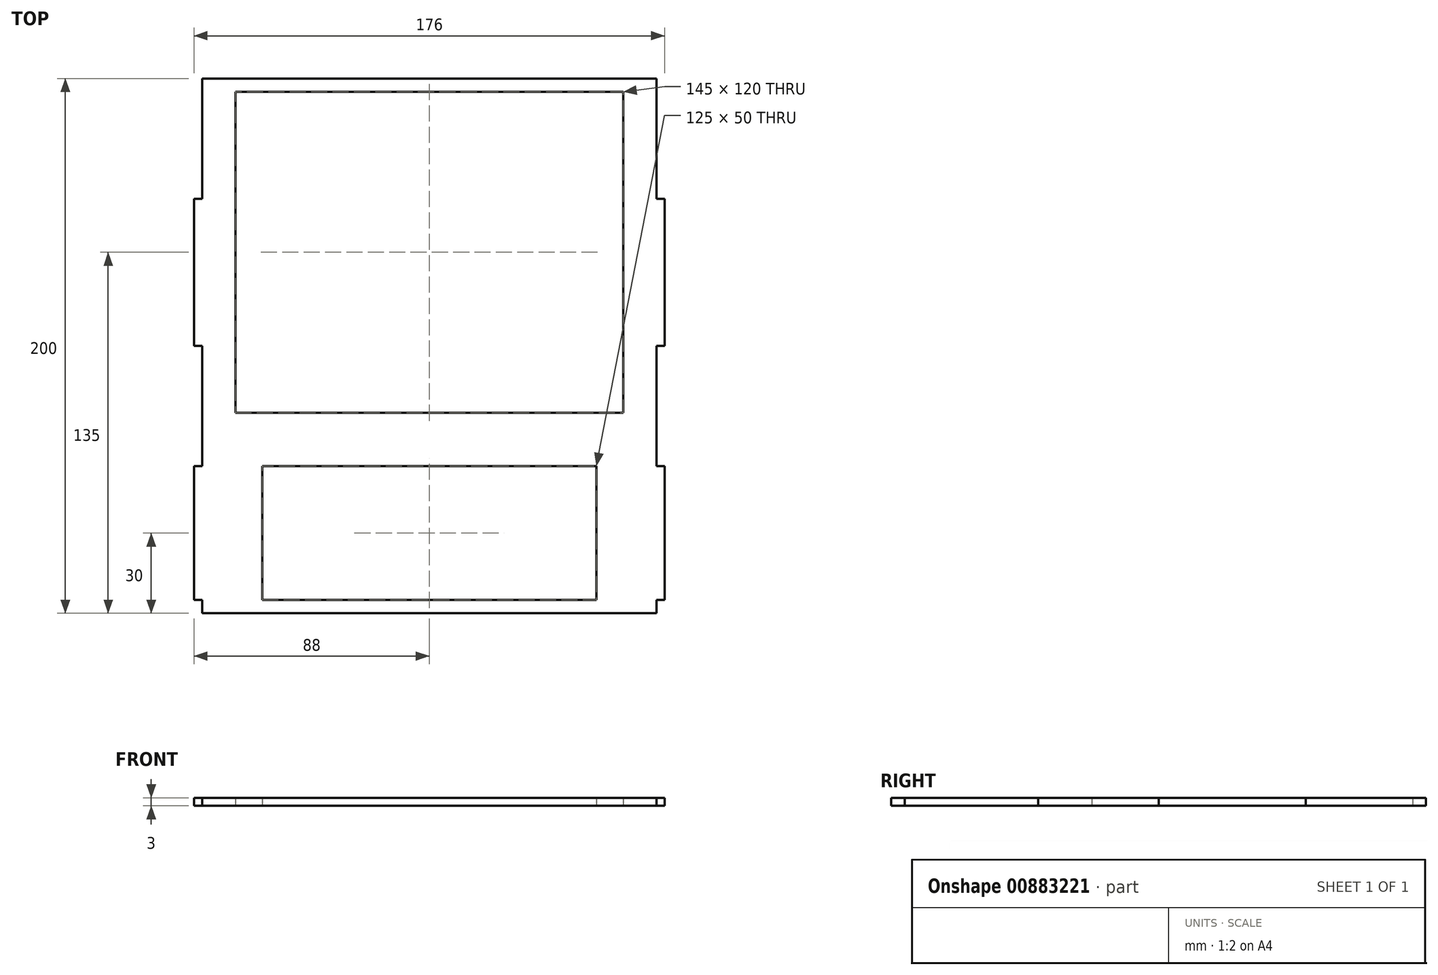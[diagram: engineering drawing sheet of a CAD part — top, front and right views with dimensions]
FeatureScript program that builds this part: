
annotation { "Feature Type Name" : "Feature", "Feature Type Description" : "" }
export const myFeature = defineFeature(function(context is Context, id is Id, definition is map)
    precondition{}
    {
        {
            var Q0;
            Q0=qCreatedBy(makeId("Top.planeOp"),FACE);
            var sketch = newSketch(context, id + "F0", { "sketchPlane" : qUnion([Q0])});
            skLineSegment(sketch, "E0.bottom", {"start": v(85, 100) * mm, "end": v(-85, 100) * mm});
            skLineSegment(sketch, "E0.top", {"start": v(85, -100) * mm, "end": v(-85, -100) * mm});
            skLineSegment(sketch, "E0.left", {"start": v(85, 100) * mm, "end": v(85, -100) * mm});
            skLineSegment(sketch, "E0.right", {"start": v(-85, 100) * mm, "end": v(-85, -100) * mm});
            skPoint(sketch, "E0.middle", {"position": v(0, 0) * mm});
            skLineSegment(sketch, "E1.bottom", {"start": v(72.5, -25) * mm, "end": v(-72.5, -25) * mm});
            skLineSegment(sketch, "E1.top", {"start": v(72.5, 95) * mm, "end": v(-72.5, 95) * mm});
            skLineSegment(sketch, "E1.left", {"start": v(72.5, -25) * mm, "end": v(72.5, 95) * mm});
            skLineSegment(sketch, "E1.right", {"start": v(-72.5, -25) * mm, "end": v(-72.5, 95) * mm});
            skPoint(sketch, "E1.middle", {"position": v(0, 35) * mm});
            skLineSegment(sketch, "E2.bottom", {"start": v(62.5, -45) * mm, "end": v(-62.5, -45) * mm});
            skLineSegment(sketch, "E2.top", {"start": v(62.5, -95) * mm, "end": v(-62.5, -95) * mm});
            skLineSegment(sketch, "E2.left", {"start": v(62.5, -45) * mm, "end": v(62.5, -95) * mm});
            skLineSegment(sketch, "E2.right", {"start": v(-62.5, -45) * mm, "end": v(-62.5, -95) * mm});
            skPoint(sketch, "E2.middle", {"position": v(0, -70) * mm});
            skLineSegment(sketch, "E3", {"start": v(85, -95) * mm, "end": v(88, -95) * mm});
            skLineSegment(sketch, "E4", {"start": v(88, -95) * mm, "end": v(88, -45) * mm});
            skLineSegment(sketch, "E5", {"start": v(88, -45) * mm, "end": v(85, -45) * mm});
            skLineSegment(sketch, "E6.MirrorCS", {"start": v(-85, -95) * mm, "end": v(-88, -95) * mm});
            skLineSegment(sketch, "E7.MirrorCS", {"start": v(-88, -45) * mm, "end": v(-85, -45) * mm});
            skLineSegment(sketch, "E8.MirrorCS", {"start": v(-88, -95) * mm, "end": v(-88, -45) * mm});
            skLineSegment(sketch, "E9", {"start": v(85, 0) * mm, "end": v(88, 0) * mm});
            skLineSegment(sketch, "E10", {"start": v(88, 0) * mm, "end": v(88, 55) * mm});
            skLineSegment(sketch, "E11", {"start": v(88, 55) * mm, "end": v(85, 55) * mm});
            skLineSegment(sketch, "E12.MirrorCS", {"start": v(-85, 0) * mm, "end": v(-88, 0) * mm});
            skLineSegment(sketch, "E13.MirrorCS", {"start": v(-88, 0) * mm, "end": v(-88, 55) * mm});
            skLineSegment(sketch, "E14.MirrorCS", {"start": v(-88, 55) * mm, "end": v(-85, 55) * mm});
            skSolve(sketch);
        }
        {
            var Q0;
            Q0 = qSketchRegion(id + "F0", true);
            extrude(context, id + "F1", {"entities" : qUnion([Q0]), "depth" : 3 * mm, "offsetDistance" : 25 * mm});
        }
    });
